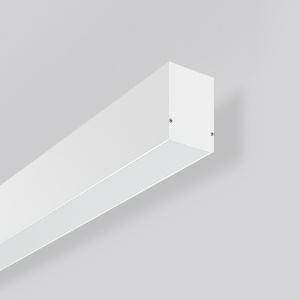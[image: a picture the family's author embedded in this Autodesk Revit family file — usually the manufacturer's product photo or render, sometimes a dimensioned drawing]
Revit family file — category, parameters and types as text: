
# Revit family: less_is_more_50_312607_002_1_76_d5f6
name_source: partatom
category: Lighting Fixtures
units: mm (PartAtom-declared; Revit-internal decimal feet)

## family parameters
Cut with Voids When Loaded = No
Host = Face
Light Source = No
Part Type = Normal
Room Calculation Point = No
Round Connector Dimension = Use Diameter
Shared = No

## types (1)
- LESS IS MORE 50 (1 x LED Modul 840, 1500 lm, 4000)
    Apparent Load = 13 VA
    CIE Flux Codes = 48 80 96 100 100
    Color Rendering = 80
    Color Temperature = 4000
    Default Elevation = 1800 mm
    Description = Series: LESS IS MORE 50
Linear wall luminaires. Housing: extruded aluminium profile, powder-coated. End cap aluminium powder-coated. Diffuser made of non-yellowing plastic (PMMA), opal. Direct light emission. Suitable for Wall (surface). LED unit with integrated converter interchangeable and removable. Suitable for through-wiring. With sensors or as a safety luminaire on request. 
Colour: traffic white, matt (RAL 9016)
Length: 1127 mm
Width: 67 mm
Height: 75 mm
Lamp: LED
Socket: without socket
Colour temperature: 4000K
Colour rendering index (CRI): 80
System power: 13 W
Rated luminous flux: 1500 lm
Luminous efficiency: 115 lm/W
Control gear: Converter, dimmable, DALI
Protection class: I
Type of protection: IP 20
    Height = 75 mm
    Lamp = 1 x LED Modul 840
    Lamp Light Flux = 1500 lm
    Lamp count = 1
    Length = 1127 mm
    Lifetime = 50000 h
    Luminous efficacy = 115 lm/W
    Manufacturer = RZB
    ModVariant = No
    Model = 312607.002.1.76
    Mounting Place = Wall
    Mounting Type = Surface mounted
    Number of Poles = 1
    OnlyDefault = Yes
    Power Factor = 1
    Product Name = LESS IS MORE 50
    Product group = Surface mounted LED linear luminaires
    ProductGroupID = 2007
    Protection Class = Protection class I
    Protection Degree = IP 20
    RLX_Detail_Level = 1
    RLX_Emergency_Light_Flux = 0 lm
    RLX_Emergency_Type = 0
    RLX_Emergency_Type_DB = No
    RlxData = <blob elided: 35157 chars, md5=3bd129bd>
    Socket = socket
    Standby Power = 0 W
    System Light Flux = 1500 lm
    System Power = 13 W
    Type Comments = Product without accessories
    Type Image = 312606.002.jpg
    URL = http://relux.com
    VarID = ---
    Voltage = 0 V
    Weight = 0.00 kg
    Width = 67 mm

## geometry (parser evidence)
native form markers: Blend x4, Sweep x9
no freeform markers — native parametric forms only
